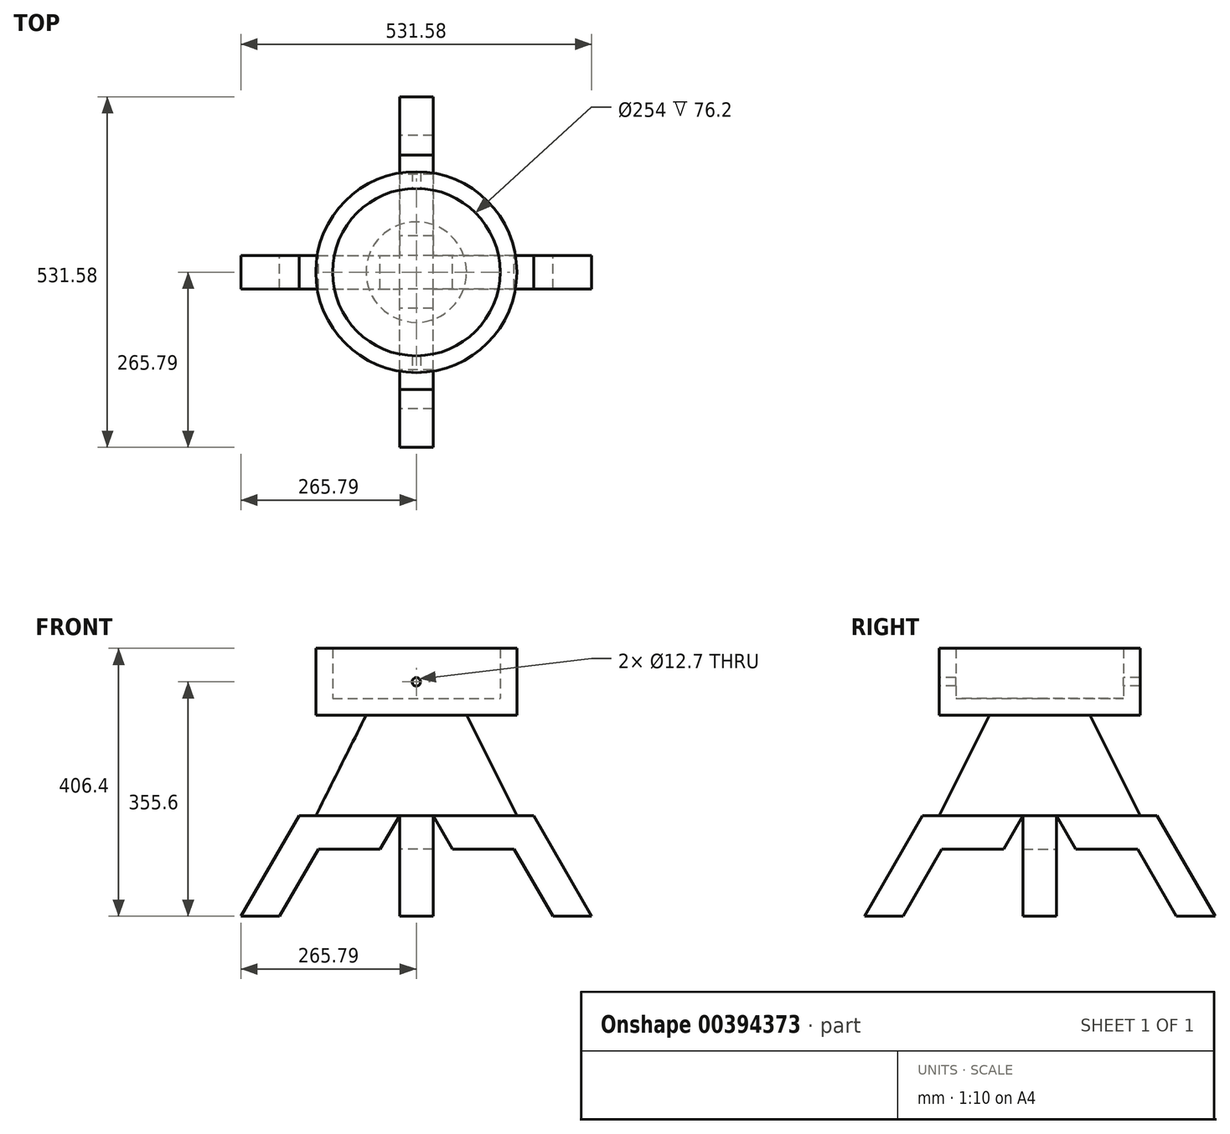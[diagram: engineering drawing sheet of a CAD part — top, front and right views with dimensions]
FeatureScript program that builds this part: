
annotation { "Feature Type Name" : "Feature", "Feature Type Description" : "" }
export const myFeature = defineFeature(function(context is Context, id is Id, definition is map)
    precondition{}
    {
        {
            var Q0;
            Q0=qCreatedBy(makeId("Top.planeOp"),FACE);
            var sketch = newSketch(context, id + "F0", { "sketchPlane" : qUnion([Q0])});
            skCircle(sketch, "E0", {"center": v(0, 0) * mm, "radius": 127 * mm});
            skCircle(sketch, "E1", {"center": v(0, 0) * mm, "radius": 152.4 * mm});
            skSolve(sketch);
        }
        {
            var Q0;
            Q0 = qSketchRegion(id + "F0", true);
            extrude(context, id + "F1", {"entities" : qUnion([Q0]), "depth" : 101.6 * mm});
        }
        {
            var Q0;
            Q0=makeQuery(id+"F1.opExtrude","CAP_FACE",FACE,{"disambiguationData":[OSD([sQuery(id+"F0.wireOp",EDGE,"E0"),sQuery(id+"F0.wireOp",EDGE,"E1")])],"isStart":true});
            var sketch = newSketch(context, id + "F2", { "sketchPlane" : qUnion([Q0])});
            skCircle(sketch, "E2", {"center": v(0, 0) * mm, "radius": 127.02 * mm});
            skSolve(sketch);
        }
        {
            var Q0;
            Q0 = qSketchRegion(id + "F2", true);
            extrude(context, id + "F3", {"entities" : qUnion([Q0]), "operationType" : NewBodyOperationType.ADD, "oppositeDirection" : true, "depth" : 25.4 * mm});
        }
        {
            var Q0;
            Q0=qCreatedBy(makeId("Front.planeOp"),FACE);
            cPlane(context, id + "F4", {"entities" : qUnion([Q0]), "cplaneType" : CPlaneType.OFFSET, "offset" : 152.4 * mm, "width" : 152.4 * mm, "height" : 152.4 * mm});
        }
        {
            var Q0;
            Q0=qCreatedBy(id+"F4.planeOp",FACE);
            var sketch = newSketch(context, id + "F5", { "sketchPlane" : qUnion([Q0])});
            skCircle(sketch, "E3", {"center": v(0, 50.8) * mm, "radius": 6.35 * mm});
            skSolve(sketch);
        }
        {
            var Q0;
            Q0 = qSketchRegion(id + "F5", true);
            extrude(context, id + "F6", {"entities" : qUnion([Q0]), "operationType" : NewBodyOperationType.REMOVE, "endBound" : BoundingType.THROUGH_ALL, "oppositeDirection" : true, "depth" : 25.4 * mm});
        }
        {
            var Q0;
            Q0=makeQuery(id+"F2.imprint","IMPRINT",FACE,{"disambiguationData":[TD([[makeQuery(id+"F2.imprint","IMPRINT",EDGE,{"derivedFrom":makeQuery(id+"F1.opExtrude","CAP_EDGE",EDGE,{"disambiguationData":[OSD([sQuery(id+"F0.wireOp",EDGE,"E0")])],"isStart":true})}),-1.0]])]});
            var sketch = newSketch(context, id + "F7", { "sketchPlane" : qUnion([Q0])});
            skCircle(sketch, "E4", {"center": v(0, 0) * mm, "radius": 76.2 * mm});
            skSolve(sketch);
        }
        {
            var Q0;
            Q0=makeQuery(id+"F2.imprint","IMPRINT",FACE,{"disambiguationData":[TD([[makeQuery(id+"F2.imprint","IMPRINT",EDGE,{"derivedFrom":makeQuery(id+"F1.opExtrude","CAP_EDGE",EDGE,{"disambiguationData":[OSD([sQuery(id+"F0.wireOp",EDGE,"E0")])],"isStart":true})}),-1.0]])]});
            cPlane(context, id + "F8", {"entities" : qUnion([Q0]), "cplaneType" : CPlaneType.OFFSET, "offset" : 152.4 * mm, "width" : 152.4 * mm, "height" : 152.4 * mm});
        }
        {
            var Q0;
            Q0=qCreatedBy(id+"F8.planeOp",FACE);
            var sketch = newSketch(context, id + "F9", { "sketchPlane" : qUnion([Q0])});
            skCircle(sketch, "E5", {"center": v(0, 0) * mm, "radius": 152.4 * mm});
            skSolve(sketch);
        }
        {
            var Q1;
            Q1=makeQuery(id+"F9.imprint","IMPRINT",FACE,{"disambiguationData":[TD([[makeQuery(id+"F9.imprint","IMPRINT",EDGE,{"derivedFrom":sQuery(id+"F9.wireOp",EDGE,"E5")}),1.0]])]});
            var Q2;
            Q2=makeQuery(id+"F7.imprint","IMPRINT",FACE,{"disambiguationData":[TD([[makeQuery(id+"F7.imprint","IMPRINT",EDGE,{"derivedFrom":sQuery(id+"F7.wireOp",EDGE,"E4")}),1.0]])]});
            loft(context, id + "F10", {"operationType" : NewBodyOperationType.ADD, "sheetProfilesArray" : [{ "sheetProfileEntities" : qUnion([Q1]) }, { "sheetProfileEntities" : qUnion([Q2]) }]});
        }
        {
            var Q0;
            Q0=makeQuery(id+"F10.opLoft","CAP_FACE",FACE,{"disambiguationData":[OSD([makeQuery(id+"F9.imprint","IMPRINT",FACE,{"disambiguationData":[TD([[makeQuery(id+"F9.imprint","IMPRINT",EDGE,{"derivedFrom":sQuery(id+"F9.wireOp",EDGE,"E5")}),1.0]])]})])],"isStart":true});
            var sketch = newSketch(context, id + "F11", { "sketchPlane" : qUnion([Q0])});
            skLineSegment(sketch, "E6", {"start": v(25.4, 0) * mm, "end": v(177.8, 0) * mm});
            skLineSegment(sketch, "E7", {"start": v(-25.4, 0) * mm, "end": v(-177.8, 0) * mm});
            skLineSegment(sketch, "E8", {"start": v(0, 25.4) * mm, "end": v(0, 177.8) * mm});
            skLineSegment(sketch, "E9", {"start": v(0, -25.4) * mm, "end": v(0, -177.8) * mm});
            skSolve(sketch);
        }
        {
            var Q0;
            Q0=qCreatedBy(makeId("Front.planeOp"),FACE);
            var sketch = newSketch(context, id + "F12", { "sketchPlane" : qUnion([Q0])});
            skLineSegment(sketch, "E10", {"start": v(207.13, -304.8) * mm, "end": v(265.79, -304.8) * mm});
            skLineSegment(sketch, "E11", {"start": v(265.79, -304.8) * mm, "end": v(177.8, -152.4) * mm});
            skLineSegment(sketch, "E12", {"start": v(207.13, -304.8) * mm, "end": v(148.47, -203.2) * mm});
            skLineSegment(sketch, "E13", {"start": v(148.47, -203.2) * mm, "end": v(54.73, -203.2) * mm});
            skLineSegment(sketch, "E14", {"start": v(54.73, -203.2) * mm, "end": v(25.4, -152.4) * mm});
            skLineSegment(sketch, "E15", {"start": v(-265.79, -304.8) * mm, "end": v(-207.13, -304.8) * mm});
            skLineSegment(sketch, "E16", {"start": v(-265.79, -304.8) * mm, "end": v(-177.8, -152.4) * mm});
            skLineSegment(sketch, "E17", {"start": v(-207.13, -304.8) * mm, "end": v(-148.47, -203.2) * mm});
            skLineSegment(sketch, "E18", {"start": v(-148.47, -203.2) * mm, "end": v(-54.73, -203.2) * mm});
            skLineSegment(sketch, "E19", {"start": v(-54.73, -203.2) * mm, "end": v(-25.4, -152.4) * mm});
            skLineSegment(sketch, "E20", {"start": v(-177.8, -152.4) * mm, "end": v(-25.4, -152.4) * mm});
            skLineSegment(sketch, "E21", {"start": v(25.4, -152.4) * mm, "end": v(177.8, -152.4) * mm});
            skSolve(sketch);
        }
        {
            var Q0;
            Q0=makeQuery(id+"F12.imprint","IMPRINT",FACE,{"disambiguationData":[TD([[makeQuery(id+"F12.imprint","IMPRINT",EDGE,{"derivedFrom":sQuery(id+"F12.wireOp",EDGE,"E15")}),1.0]])]});
            var Q1;
            Q1=makeQuery(id+"F12.imprint","IMPRINT",FACE,{"disambiguationData":[TD([[makeQuery(id+"F12.imprint","IMPRINT",EDGE,{"derivedFrom":sQuery(id+"F12.wireOp",EDGE,"E10")}),1.0]])]});
            extrude(context, id + "F13", {"entities" : qUnion([Q0, Q1]), "operationType" : NewBodyOperationType.ADD, "endBound" : BoundingType.SYMMETRIC, "depth" : 50.8 * mm});
        }
        {
            var Q0;
            Q0=qCreatedBy(makeId("Right.planeOp"),FACE);
            var sketch = newSketch(context, id + "F14", { "sketchPlane" : qUnion([Q0])});
            skLineSegment(sketch, "E22", {"start": v(-177.8, -152.4) * mm, "end": v(-265.79, -304.8) * mm});
            skLineSegment(sketch, "E23", {"start": v(-265.79, -304.8) * mm, "end": v(-207.13, -304.8) * mm});
            skLineSegment(sketch, "E24", {"start": v(-207.13, -304.8) * mm, "end": v(-148.47, -203.2) * mm});
            skLineSegment(sketch, "E25", {"start": v(-148.47, -203.2) * mm, "end": v(-54.73, -203.2) * mm});
            skLineSegment(sketch, "E26", {"start": v(-54.73, -203.2) * mm, "end": v(-25.4, -152.4) * mm});
            skLineSegment(sketch, "E27", {"start": v(-177.8, -152.4) * mm, "end": v(-25.4, -152.4) * mm});
            skLineSegment(sketch, "E28", {"start": v(177.8, -152.4) * mm, "end": v(265.79, -304.8) * mm});
            skLineSegment(sketch, "E29", {"start": v(265.79, -304.8) * mm, "end": v(207.13, -304.8) * mm});
            skLineSegment(sketch, "E30", {"start": v(207.13, -304.8) * mm, "end": v(148.47, -203.2) * mm});
            skLineSegment(sketch, "E31", {"start": v(148.47, -203.2) * mm, "end": v(54.73, -203.2) * mm});
            skLineSegment(sketch, "E32", {"start": v(54.73, -203.2) * mm, "end": v(25.4, -152.4) * mm});
            skLineSegment(sketch, "E33", {"start": v(25.4, -152.4) * mm, "end": v(177.8, -152.4) * mm});
            skSolve(sketch);
        }
        {
            var Q0;
            Q0=makeQuery(id+"F14.imprint","IMPRINT",FACE,{"disambiguationData":[TD([[makeQuery(id+"F14.imprint","IMPRINT",EDGE,{"derivedFrom":sQuery(id+"F14.wireOp",EDGE,"E22")}),1.0]])]});
            var Q1;
            Q1=makeQuery(id+"F14.imprint","IMPRINT",FACE,{"disambiguationData":[TD([[makeQuery(id+"F14.imprint","IMPRINT",EDGE,{"derivedFrom":sQuery(id+"F14.wireOp",EDGE,"E28")}),-1.0]])]});
            extrude(context, id + "F15", {"entities" : qUnion([Q0, Q1]), "operationType" : NewBodyOperationType.ADD, "endBound" : BoundingType.SYMMETRIC, "depth" : 50.8 * mm});
        }
    });
